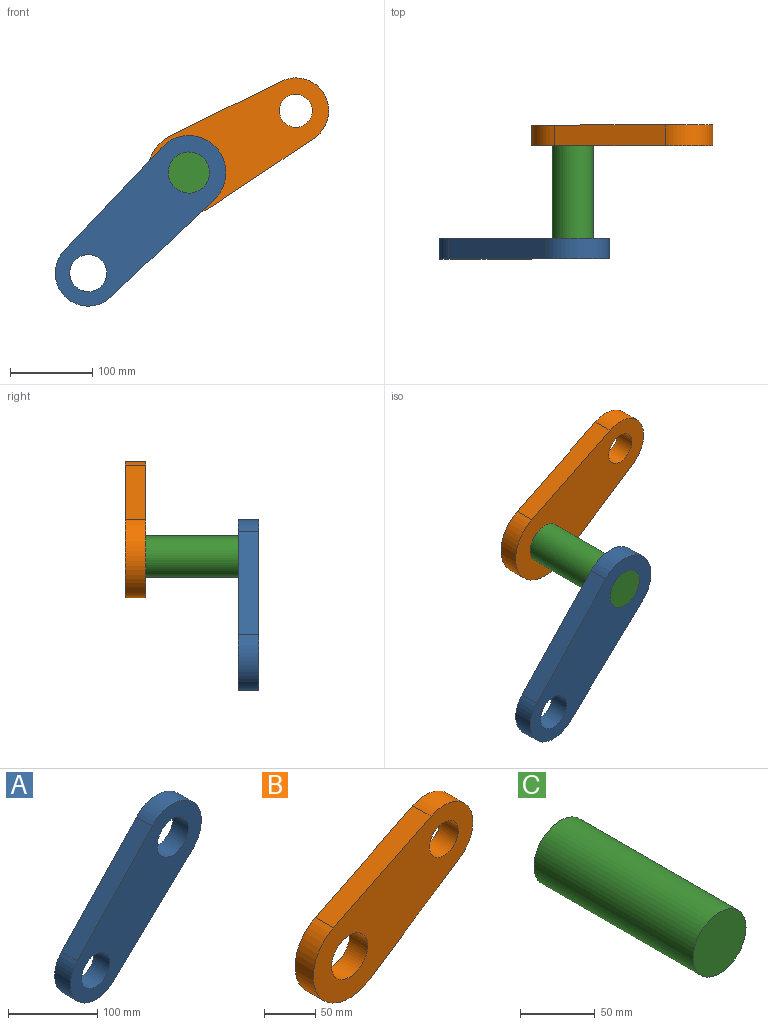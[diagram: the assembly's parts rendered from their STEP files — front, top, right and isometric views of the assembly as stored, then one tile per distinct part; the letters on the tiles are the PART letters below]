
ASSEMBLY  parts=3 mates=2
PART A: 8 faces, bbox 207.3x25x207.3 mm
  f0: cylinder r=45mm len=77.73mm, axis (0,1,0), area 3599.4mm2, adj f1,f3,f6,f7
  f1: plane 125.69x118.62mm, normal (-0.73,0,0.69), area 4320.6mm2, adj f0,f2,f6,f7
  f2: cylinder r=40mm len=67.45mm, axis (0,1,0), area 3083.7mm2, adj f1,f3,f6,f7
  f3: plane 125.69x118.62mm, normal (0.69,0,-0.73), area 4320.6mm2, adj f0,f2,f6,f7
  f4: cylinder r=25mm len=50mm, axis (0,1,0), area 3927mm2, adj f6,f7
  f5: cylinder r=22.5mm len=45mm, axis (0,1,0), area 3534.3mm2, adj f6,f7
  f6: plane 207.26x207.26mm, normal (0,-1,0), area 16842.7mm2, adj f0,f1,f2,f3,f4,f5
  f7: plane 207.26x207.26mm, normal (0,1,0), area 16842.7mm2, adj f0,f1,f2,f3,f4,f5
PART B: 8 faces, bbox 219.9x25x165 mm
  f0: cylinder r=50mm len=94.87mm, axis (0,1,0), area 4093.8mm2, adj f1,f3,f6,f7
  f1: plane 124.34x83.31mm, normal (0.56,0,-0.83), area 3741.7mm2, adj f0,f2,f6,f7
  f2: cylinder r=40mm len=73.23mm, axis (0,1,0), area 3008.2mm2, adj f1,f3,f6,f7
  f3: plane 134.32x66.03mm, normal (-0.44,0,0.9), area 3741.7mm2, adj f0,f2,f6,f7
  f4: cylinder r=25mm len=50mm, axis (0,1,0), area 3927mm2, adj f6,f7
  f5: cylinder r=20mm len=40mm, axis (0,1,0), area 3141.6mm2, adj f6,f7
  f6: plane 219.9x165mm, normal (0,-1,0), area 16750.1mm2, adj f0,f1,f2,f3,f4,f5
  f7: plane 219.9x165mm, normal (0,1,0), area 16750.1mm2, adj f0,f1,f2,f3,f4,f5
PART C: 3 faces, bbox 50x150x50 mm
  f0: cylinder r=25mm len=150mm, axis (0,1,0), area 23561.9mm2, adj f1,f2
  f1: plane 50x50mm, normal (0,-1,0), area 1963.5mm2, adj f0
  f2: plane 50x50mm, normal (0,1,0), area 1963.5mm2, adj f0
PLACE A t=(11.95,18.49,17.39)mm
PLACE B t=(11.95,155.99,17.39)mm
PLACE C t=(11.95,143.49,17.39)mm
MATE fastened B.f0 <-> C.f0  axis (0,1,0) through (11.95,143.49,17.39)mm
MATE fastened C.f0 <-> A.f0  axis (0,-1,0) through (11.95,-6.51,17.39)mm
